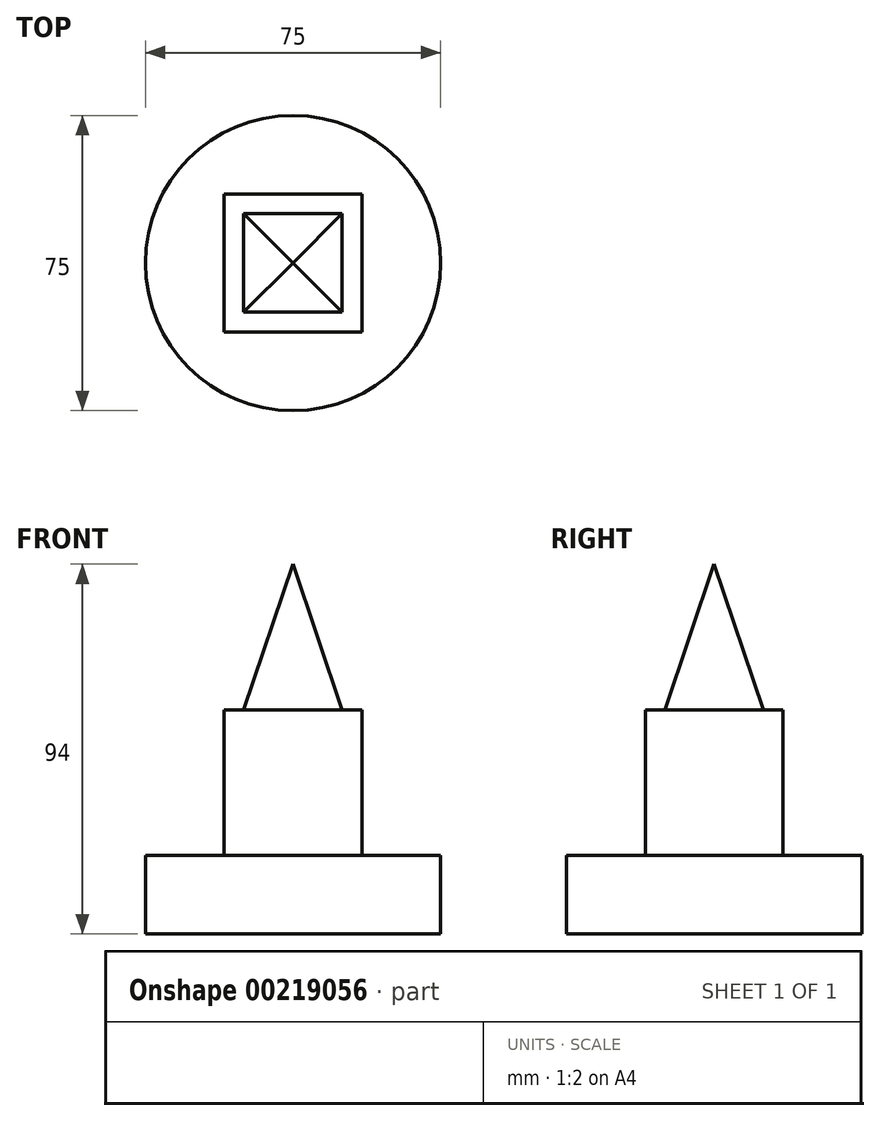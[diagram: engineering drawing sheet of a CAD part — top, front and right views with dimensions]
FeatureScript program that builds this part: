
annotation { "Feature Type Name" : "Feature", "Feature Type Description" : "" }
export const myFeature = defineFeature(function(context is Context, id is Id, definition is map)
    precondition{}
    {
        {
            var Q0;
            Q0=qCreatedBy(makeId("Front.planeOp"),FACE);
            var sketch = newSketch(context, id + "F0", { "sketchPlane" : qUnion([Q0])});
            skLineSegment(sketch, "E0", {"start": v(0, 0) * mm, "end": v(37.5, 0) * mm});
            skLineSegment(sketch, "E1", {"start": v(37.5, 0) * mm, "end": v(37.5, 20) * mm});
            skLineSegment(sketch, "E2", {"start": v(37.5, 20) * mm, "end": v(17.5, 20) * mm});
            skLineSegment(sketch, "E3", {"start": v(17.5, 20) * mm, "end": v(17.5, 57) * mm});
            skLineSegment(sketch, "E4", {"start": v(17.5, 57) * mm, "end": v(12.5, 57) * mm});
            skLineSegment(sketch, "E5", {"start": v(0, 94) * mm, "end": v(0, 0) * mm});
            skLineSegment(sketch, "E6", {"start": v(12.5, 57) * mm, "end": v(0, 57) * mm});
            skLineSegment(sketch, "E7", {"start": v(17.5, 20) * mm, "end": v(0, 20) * mm});
            skSolve(sketch);
        }
        {
            var Q0;
            {var subQ1=sQuery(id+"F0.wireOp",EDGE,"E0");Q0=makeQuery(id+"F0.imprint","IMPRINT",FACE,{"disambiguationData":[TD([[makeQuery(id+"F0.imprint","IMPRINT",EDGE,{"derivedFrom":subQ1}),1.0]])]});}
            var Q1;
            Q1=sQuery(id+"F0.wireOp",EDGE,"E5");
            revolve(context, id + "F1", {"entities" : qUnion([Q0]), "axis" : qUnion([Q1]), "revolveType" : RevolveType.FULL});
        }
        {
            var Q0;
            Q0=makeQuery(id+"F0.imprint","IMPRINT",FACE,{"disambiguationData":[TD([[makeQuery(id+"F0.imprint","IMPRINT",EDGE,{"derivedFrom":sQuery(id+"F0.wireOp",EDGE,"E3")}),1.0]])]});
            extrude(context, id + "F2", {"entities" : qUnion([Q0]), "operationType" : NewBodyOperationType.ADD, "endBound" : BoundingType.SYMMETRIC, "depth" : 35 * mm});
        }
        {
            var Q0;
            Q0=makeQuery(id+"F2.opExtrude","SWEPT_FACE",FACE,{"disambiguationData":[OSD([sQuery(id+"F0.wireOp",EDGE,"E4"),sQuery(id+"F0.wireOp",EDGE,"E6")])]});
            var sketch = newSketch(context, id + "F3", { "sketchPlane" : qUnion([Q0])});
            skLineSegment(sketch, "E8.bottom", {"start": v(0, 12.5) * mm, "end": v(12.5, 12.5) * mm});
            skLineSegment(sketch, "E8.top", {"start": v(0, -12.5) * mm, "end": v(12.5, -12.5) * mm});
            skLineSegment(sketch, "E8.left", {"start": v(0, 12.5) * mm, "end": v(0, -12.5) * mm});
            skLineSegment(sketch, "E8.right", {"start": v(12.5, 12.5) * mm, "end": v(12.5, -12.5) * mm});
            skSolve(sketch);
        }
        {
            var Q0;
            {var subQ6=sQuery(id+"F3.wireOp",EDGE,"E8.bottom");Q0=makeQuery(id+"F3.imprint","IMPRINT",FACE,{"disambiguationData":[TD([[makeQuery(id+"F3.imprint","IMPRINT",EDGE,{"derivedFrom":subQ6}),1.0]])]});}
            cPlane(context, id + "F4", {"entities" : qUnion([Q0]), "cplaneType" : CPlaneType.OFFSET, "offset" : 37 * mm, "width" : 150 * mm, "height" : 150 * mm});
        }
        {
            var Q0;
            Q0=qCreatedBy(id+"F4.planeOp",FACE);
            var sketch = newSketch(context, id + "F5", { "sketchPlane" : qUnion([Q0])});
            skPoint(sketch, "E9", {"position": v(0, 0) * mm});
            skSolve(sketch);
        }
        {
            var Q1;
            Q1=makeQuery(id+"F3.imprint","IMPRINT",FACE,{"disambiguationData":[TD([[makeQuery(id+"F3.imprint","IMPRINT",EDGE,{"derivedFrom":sQuery(id+"F3.wireOp",EDGE,"E8.bottom")}),-1.0]])]});
            var Q2;
            Q2=sQuery(id+"F5.wireOp",VERTEX,"E9");
            loft(context, id + "F6", {"operationType" : NewBodyOperationType.ADD, "sheetProfilesArray" : [{ "sheetProfileEntities" : qUnion([Q1]) }, { "sheetProfileEntities" : qUnion([Q2]) }]});
        }
        {
            var Q0;
            Q0=makeQuery(id+"F1.opRevolve","SWEPT_BODY",BODY,{"disambiguationData":[OSD([sQuery(id+"F0.wireOp",EDGE,"E0"),sQuery(id+"F0.wireOp",EDGE,"E1"),sQuery(id+"F0.wireOp",EDGE,"E2"),sQuery(id+"F0.wireOp",EDGE,"E5"),sQuery(id+"F0.wireOp",EDGE,"E7")])]});
            var Q1;
            Q1=qCreatedBy(makeId("Right.planeOp"),FACE);
            mirror(context, id + "F7", {"operationType" : NewBodyOperationType.ADD, "entities" : qUnion([Q0]), "mirrorPlane" : qUnion([Q1])});
        }
    });
